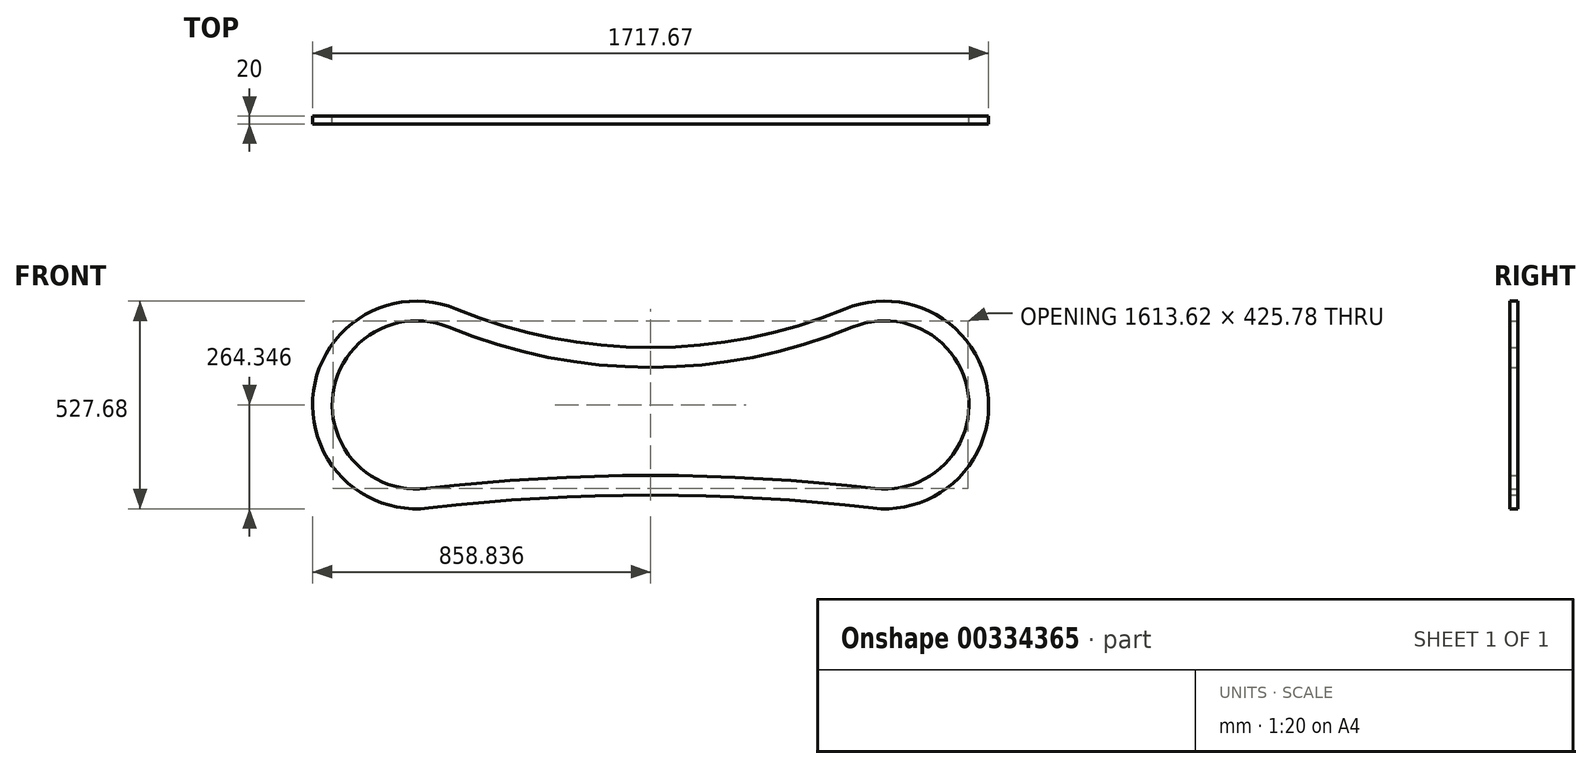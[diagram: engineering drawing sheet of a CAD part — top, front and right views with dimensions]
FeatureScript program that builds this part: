
annotation { "Feature Type Name" : "Feature", "Feature Type Description" : "" }
export const myFeature = defineFeature(function(context is Context, id is Id, definition is map)
    precondition{}
    {
        {
            var Q0;
            Q0=qCreatedBy(makeId("Front.planeOp"),FACE);
            var sketch = newSketch(context, id + "F0", { "sketchPlane" : qUnion([Q0])});
            skArc(sketch, "E0", {"start": v(-501.04, 243.8) * mm, "mid": v(-863.21, 36.23) * mm, "end": v(-571.18, -262.05) * mm});
            skArc(sketch, "E1", {"start": v(557.43, -262.05) * mm, "mid": v(849.46, 36.23) * mm, "end": v(487.3, 243.8) * mm});
            skLineSegment(sketch, "E2", {"start": v(-601.87, 0) * mm, "end": v(588.13, 0) * mm});
            skArc(sketch, "E3", {"start": v(557.43, -262.05) * mm, "mid": v(-6.87, -229.1) * mm, "end": v(-571.18, -262.05) * mm});
            skPoint(sketch, "E3.centerSnap0", {"position": v(-6.87, 0) * mm});
            skArc(sketch, "E4", {"start": v(-501.04, 243.8) * mm, "mid": v(-6.87, 145.65) * mm, "end": v(487.3, 243.8) * mm});
            skArc(sketch, "E5.0", {"start": v(-520.15, 197.6) * mm, "mid": v(-6.87, 95.65) * mm, "end": v(506.4, 197.6) * mm});
            skArc(sketch, "E5.1", {"start": v(-520.15, 197.6) * mm, "mid": v(-813.69, 29.37) * mm, "end": v(-577, -212.39) * mm});
            skArc(sketch, "E5.2", {"start": v(563.25, -212.39) * mm, "mid": v(-6.87, -179.1) * mm, "end": v(-577, -212.39) * mm});
            skArc(sketch, "E5.3", {"start": v(563.25, -212.39) * mm, "mid": v(799.94, 29.37) * mm, "end": v(506.4, 197.6) * mm});
            skSolve(sketch);
        }
        {
            var Q0;
            Q0=makeQuery(id+"F0.imprint","IMPRINT",FACE,{"disambiguationData":[TD([[makeQuery(id+"F0.imprint","IMPRINT",EDGE,{"derivedFrom":sQuery(id+"F0.wireOp",EDGE,"E0")}),1.0]])]});
            extrude(context, id + "F1", {"entities" : qUnion([Q0]), "depth" : 20 * mm});
        }
    });
